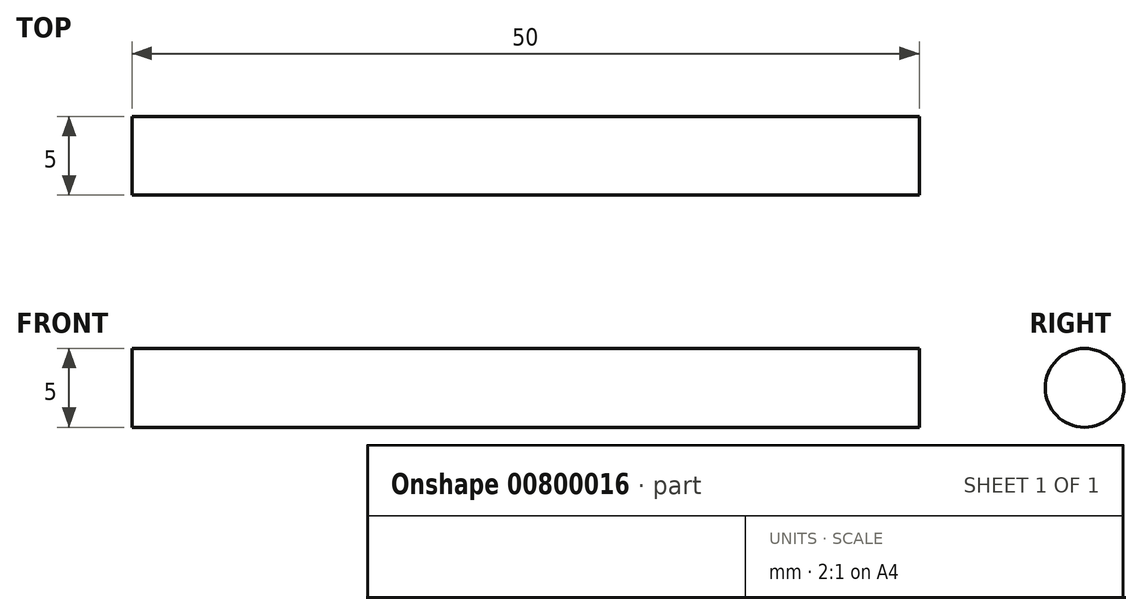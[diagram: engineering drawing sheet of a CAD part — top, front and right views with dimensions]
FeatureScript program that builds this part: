
annotation { "Feature Type Name" : "Feature", "Feature Type Description" : "" }
export const myFeature = defineFeature(function(context is Context, id is Id, definition is map)
    precondition{}
    {
        {
            var Q0;
            Q0=qCreatedBy(makeId("Right.planeOp"),FACE);
            var sketch = newSketch(context, id + "F0", { "sketchPlane" : qUnion([Q0])});
            skSolve(sketch);
        }
        {
            var Q0;
            Q0=qCreatedBy(makeId("Right.planeOp"),FACE);
            var sketch = newSketch(context, id + "F1", { "sketchPlane" : qUnion([Q0])});
            skCircle(sketch, "E0", {"center": v(0, 0) * mm, "radius": 2.5 * mm});
            skSolve(sketch);
        }
        {
            var Q0;
            Q0 = qSketchRegion(id + "F0", true);
            var Q1;
            Q1=makeQuery(id+"F1.imprint","IMPRINT",FACE,{"disambiguationData":[TD([[makeQuery(id+"F1.imprint","IMPRINT",EDGE,{"derivedFrom":sQuery(id+"F1.wireOp",EDGE,"E0")}),1.0]])]});
            extrude(context, id + "F2", {"entities" : qUnion([Q0, Q1]), "depth" : 50 * mm, "offsetDistance" : 25.4 * mm});
        }
        {
            var Q0;
            Q0=makeQuery(id+"F2.opExtrude","SWEPT_BODY",BODY,{"disambiguationData":[OSD([sQuery(id+"F1.wireOp",EDGE,"E0")])]});
            transform(context, id + "F3", {"entities" : qUnion([Q0]), "transformType" : TransformType.TRANSLATION_3D, "dx" : 0 * mm, "dy" : 0 * mm, "dz" : 0 * mm, "makeCopy" : true});
        }
        {
            var Q0;
            Q0=makeQuery(id+"F2.opExtrude","SWEPT_BODY",BODY,{"disambiguationData":[OSD([sQuery(id+"F1.wireOp",EDGE,"E0")])]});
            deleteBodies(context, id + "F4", {"entities" : qUnion([Q0])});
        }
    });
